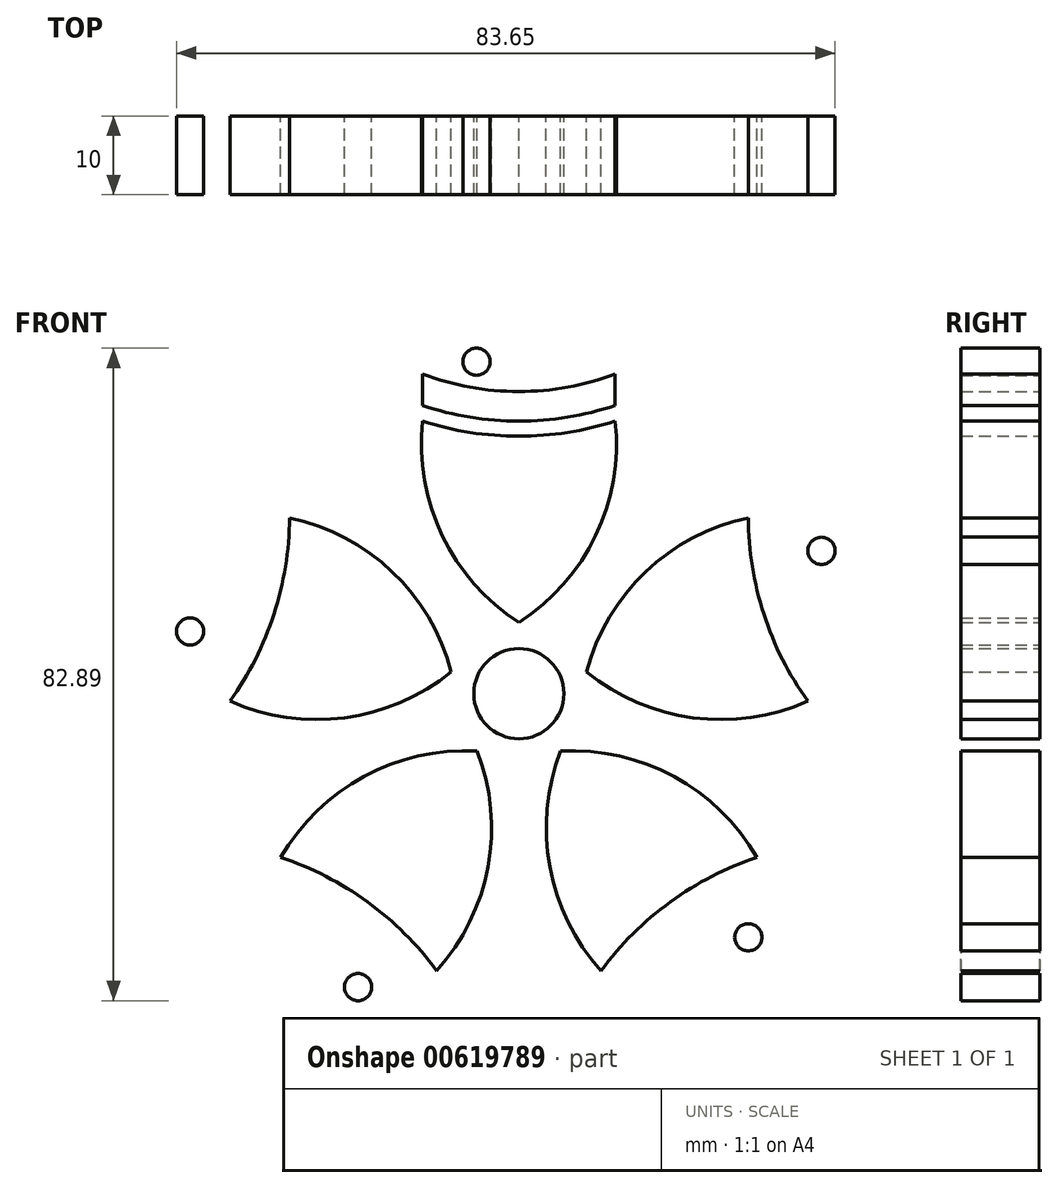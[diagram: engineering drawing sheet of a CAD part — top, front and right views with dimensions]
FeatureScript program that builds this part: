
annotation { "Feature Type Name" : "Feature", "Feature Type Description" : "" }
export const myFeature = defineFeature(function(context is Context, id is Id, definition is map)
    precondition{}
    {
        {
            var Q0;
            Q0=qCreatedBy(makeId("Front.planeOp"),FACE);
            var sketch = newSketch(context, id + "F0", { "sketchPlane" : qUnion([Q0])});
            skLineSegment(sketch, "E0", {"start": v(0, 45.42) * mm, "end": v(0, -45.42) * mm, "construction": true});
            skLineSegment(sketch, "E1", {"start": v(-45.42, 0) * mm, "end": v(45.42, 0) * mm, "construction": true});
            skCircle(sketch, "E2", {"center": v(0, 0) * mm, "radius": 5.72 * mm});
            skArc(sketch, "E3", {"start": v(-12.24, 34.62) * mm, "mid": v(-9.74, 20.09) * mm, "end": v(0, 9.03) * mm});
            skArc(sketch, "E4", {"start": v(-12.24, 34.62) * mm, "mid": v(-6.2, 33.19) * mm, "end": v(0, 32.72) * mm});
            skArc(sketch, "E5", {"start": v(-12.24, 36.62) * mm, "mid": v(-6.2, 35.11) * mm, "end": v(0, 34.62) * mm});
            skArc(sketch, "E6", {"start": v(-12.24, 40.62) * mm, "mid": v(-6.22, 38.94) * mm, "end": v(0, 38.38) * mm});
            skLineSegment(sketch, "E7", {"start": v(-12.24, 40.62) * mm, "end": v(-12.24, 36.62) * mm});
            skArc(sketch, "E8.MirrorCS", {"start": v(12.24, 34.62) * mm, "mid": v(9.74, 20.09) * mm, "end": v(0, 9.03) * mm});
            skArc(sketch, "E9.MirrorCS", {"start": v(12.24, 34.62) * mm, "mid": v(6.2, 33.19) * mm, "end": v(0, 32.72) * mm});
            skArc(sketch, "E10.MirrorCS", {"start": v(12.24, 36.62) * mm, "mid": v(6.2, 35.11) * mm, "end": v(0, 34.62) * mm});
            skArc(sketch, "E11.MirrorCS", {"start": v(12.24, 40.62) * mm, "mid": v(6.22, 38.94) * mm, "end": v(0, 38.38) * mm});
            skLineSegment(sketch, "E12.MirrorCS", {"start": v(12.24, 40.62) * mm, "end": v(12.24, 36.62) * mm});
            skArc(sketch, "E13.1.0", {"start": v(-36.7, -0.94) * mm, "mid": v(-33.48, 4.37) * mm, "end": v(-31.11, 10.1) * mm});
            skArc(sketch, "E13.1.1", {"start": v(-36.7, -0.94) * mm, "mid": v(-22.12, -3.06) * mm, "end": v(-8.59, 2.8) * mm});
            skArc(sketch, "E13.1.2", {"start": v(-29.14, 22.33) * mm, "mid": v(-16.1, 15.48) * mm, "end": v(-8.59, 2.8) * mm});
            skArc(sketch, "E13.1.3", {"start": v(-29.14, 22.33) * mm, "mid": v(-29.65, 16.14) * mm, "end": v(-31.11, 10.1) * mm});
            skArc(sketch, "E13.1.4", {"start": v(-31.04, 22.95) * mm, "mid": v(-31.48, 16.75) * mm, "end": v(-32.92, 10.7) * mm});
            skLineSegment(sketch, "E13.1.5", {"start": v(-34.85, 24.19) * mm, "end": v(-31.04, 22.95) * mm});
            skArc(sketch, "E13.1.6", {"start": v(-34.85, 24.19) * mm, "mid": v(-35.1, 17.95) * mm, "end": v(-36.5, 11.86) * mm});
            skArc(sketch, "E13.1.7", {"start": v(-42.4, 0.91) * mm, "mid": v(-38.95, 6.12) * mm, "end": v(-36.5, 11.86) * mm});
            skArc(sketch, "E13.1.8", {"start": v(-38.6, -0.32) * mm, "mid": v(-35.3, 4.95) * mm, "end": v(-32.92, 10.7) * mm});
            skLineSegment(sketch, "E13.1.9", {"start": v(-42.4, 0.91) * mm, "end": v(-38.6, -0.32) * mm});
            skArc(sketch, "E13.2.0", {"start": v(-10.45, -35.2) * mm, "mid": v(-14.5, -30.49) * mm, "end": v(-19.23, -26.47) * mm});
            skArc(sketch, "E13.2.1", {"start": v(-10.45, -35.2) * mm, "mid": v(-3.92, -21.98) * mm, "end": v(-5.3, -7.3) * mm});
            skArc(sketch, "E13.2.2", {"start": v(-30.25, -20.81) * mm, "mid": v(-19.7, -10.52) * mm, "end": v(-5.3, -7.3) * mm});
            skArc(sketch, "E13.2.3", {"start": v(-30.25, -20.81) * mm, "mid": v(-24.52, -23.2) * mm, "end": v(-19.23, -26.47) * mm});
            skArc(sketch, "E13.2.4", {"start": v(-31.42, -22.43) * mm, "mid": v(-25.65, -24.76) * mm, "end": v(-20.35, -28) * mm});
            skLineSegment(sketch, "E13.2.5", {"start": v(-33.77, -25.67) * mm, "end": v(-31.42, -22.43) * mm});
            skArc(sketch, "E13.2.6", {"start": v(-33.77, -25.67) * mm, "mid": v(-27.92, -27.84) * mm, "end": v(-22.56, -31.05) * mm});
            skArc(sketch, "E13.2.7", {"start": v(-13.97, -40.05) * mm, "mid": v(-17.85, -35.16) * mm, "end": v(-22.56, -31.05) * mm});
            skArc(sketch, "E13.2.8", {"start": v(-11.62, -36.81) * mm, "mid": v(-15.62, -32.05) * mm, "end": v(-20.35, -28) * mm});
            skLineSegment(sketch, "E13.2.9", {"start": v(-13.97, -40.05) * mm, "end": v(-11.62, -36.81) * mm});
            skArc(sketch, "E13.3.0", {"start": v(30.25, -20.81) * mm, "mid": v(24.52, -23.2) * mm, "end": v(19.23, -26.47) * mm});
            skArc(sketch, "E13.3.1", {"start": v(30.25, -20.81) * mm, "mid": v(19.7, -10.52) * mm, "end": v(5.3, -7.3) * mm});
            skArc(sketch, "E13.3.2", {"start": v(10.45, -35.2) * mm, "mid": v(3.92, -21.98) * mm, "end": v(5.3, -7.3) * mm});
            skArc(sketch, "E13.3.3", {"start": v(10.45, -35.2) * mm, "mid": v(14.5, -30.49) * mm, "end": v(19.23, -26.47) * mm});
            skArc(sketch, "E13.3.4", {"start": v(11.62, -36.81) * mm, "mid": v(15.62, -32.05) * mm, "end": v(20.35, -28) * mm});
            skLineSegment(sketch, "E13.3.5", {"start": v(13.97, -40.05) * mm, "end": v(11.62, -36.81) * mm});
            skArc(sketch, "E13.3.6", {"start": v(13.97, -40.05) * mm, "mid": v(17.85, -35.16) * mm, "end": v(22.56, -31.05) * mm});
            skArc(sketch, "E13.3.7", {"start": v(33.77, -25.67) * mm, "mid": v(27.92, -27.84) * mm, "end": v(22.56, -31.05) * mm});
            skArc(sketch, "E13.3.8", {"start": v(31.42, -22.43) * mm, "mid": v(25.65, -24.76) * mm, "end": v(20.35, -28) * mm});
            skLineSegment(sketch, "E13.3.9", {"start": v(33.77, -25.67) * mm, "end": v(31.42, -22.43) * mm});
            skArc(sketch, "E13.4.0", {"start": v(29.14, 22.33) * mm, "mid": v(29.65, 16.14) * mm, "end": v(31.11, 10.1) * mm});
            skArc(sketch, "E13.4.1", {"start": v(29.14, 22.33) * mm, "mid": v(16.1, 15.48) * mm, "end": v(8.59, 2.8) * mm});
            skArc(sketch, "E13.4.2", {"start": v(36.7, -0.94) * mm, "mid": v(22.12, -3.06) * mm, "end": v(8.59, 2.8) * mm});
            skArc(sketch, "E13.4.3", {"start": v(36.7, -0.94) * mm, "mid": v(33.48, 4.37) * mm, "end": v(31.11, 10.1) * mm});
            skArc(sketch, "E13.4.4", {"start": v(38.6, -0.32) * mm, "mid": v(35.3, 4.95) * mm, "end": v(32.92, 10.7) * mm});
            skLineSegment(sketch, "E13.4.5", {"start": v(42.4, 0.91) * mm, "end": v(38.6, -0.32) * mm});
            skArc(sketch, "E13.4.6", {"start": v(42.4, 0.91) * mm, "mid": v(38.95, 6.12) * mm, "end": v(36.5, 11.86) * mm});
            skArc(sketch, "E13.4.7", {"start": v(34.85, 24.19) * mm, "mid": v(35.1, 17.95) * mm, "end": v(36.5, 11.86) * mm});
            skArc(sketch, "E13.4.8", {"start": v(31.04, 22.95) * mm, "mid": v(31.48, 16.75) * mm, "end": v(32.92, 10.7) * mm});
            skLineSegment(sketch, "E13.4.9", {"start": v(34.85, 24.19) * mm, "end": v(31.04, 22.95) * mm});
            skCircle(sketch, "E14", {"center": v(-5.39, 42.17) * mm, "radius": 1.73 * mm});
            skCircle(sketch, "E15.MirrorC", {"center": v(5.39, 42.17) * mm, "radius": 1.73 * mm});
            skCircle(sketch, "E16.1.0", {"center": v(-41.77, 7.9) * mm, "radius": 1.73 * mm});
            skCircle(sketch, "E16.1.1", {"center": v(-38.44, 18.15) * mm, "radius": 1.73 * mm});
            skCircle(sketch, "E16.2.0", {"center": v(-20.43, -37.28) * mm, "radius": 1.73 * mm});
            skCircle(sketch, "E16.2.1", {"center": v(-29.14, -30.95) * mm, "radius": 1.73 * mm});
            skCircle(sketch, "E16.3.0", {"center": v(29.14, -30.95) * mm, "radius": 1.73 * mm});
            skCircle(sketch, "E16.3.1", {"center": v(20.43, -37.28) * mm, "radius": 1.73 * mm});
            skCircle(sketch, "E16.4.0", {"center": v(38.44, 18.15) * mm, "radius": 1.73 * mm});
            skCircle(sketch, "E16.4.1", {"center": v(41.77, 7.9) * mm, "radius": 1.73 * mm});
            skSolve(sketch);
        }
        {
            var Q0;
            Q0=makeQuery(id+"F0.imprint","IMPRINT",FACE,{"disambiguationData":[TD([[makeQuery(id+"F0.imprint","IMPRINT",EDGE,{"derivedFrom":sQuery(id+"F0.wireOp",EDGE,"E13.1.0")}),-1.0]])]});
            var Q1;
            Q1=makeQuery(id+"F0.imprint","IMPRINT",FACE,{"disambiguationData":[TD([[makeQuery(id+"F0.imprint","IMPRINT",EDGE,{"derivedFrom":sQuery(id+"F0.wireOp",EDGE,"E13.1.4")}),-1.0]])]});
            var Q2;
            Q2=makeQuery(id+"F0.imprint","IMPRINT",FACE,{"disambiguationData":[TD([[makeQuery(id+"F0.imprint","IMPRINT",EDGE,{"derivedFrom":sQuery(id+"F0.wireOp",EDGE,"E3")}),1.0]])]});
            var Q3;
            Q3=makeQuery(id+"F0.imprint","IMPRINT",FACE,{"disambiguationData":[TD([[makeQuery(id+"F0.imprint","IMPRINT",EDGE,{"derivedFrom":sQuery(id+"F0.wireOp",EDGE,"E5")}),1.0]])]});
            var Q4;
            Q4=makeQuery(id+"F0.imprint","IMPRINT",FACE,{"disambiguationData":[TD([[makeQuery(id+"F0.imprint","IMPRINT",EDGE,{"derivedFrom":sQuery(id+"F0.wireOp",EDGE,"E13.4.0")}),-1.0]])]});
            var Q5;
            Q5=makeQuery(id+"F0.imprint","IMPRINT",FACE,{"disambiguationData":[TD([[makeQuery(id+"F0.imprint","IMPRINT",EDGE,{"derivedFrom":sQuery(id+"F0.wireOp",EDGE,"E13.4.4")}),-1.0]])]});
            var Q6;
            Q6=makeQuery(id+"F0.imprint","IMPRINT",FACE,{"disambiguationData":[TD([[makeQuery(id+"F0.imprint","IMPRINT",EDGE,{"derivedFrom":sQuery(id+"F0.wireOp",EDGE,"E13.3.0")}),-1.0]])]});
            var Q7;
            Q7=makeQuery(id+"F0.imprint","IMPRINT",FACE,{"disambiguationData":[TD([[makeQuery(id+"F0.imprint","IMPRINT",EDGE,{"derivedFrom":sQuery(id+"F0.wireOp",EDGE,"E13.3.4")}),-1.0]])]});
            var Q8;
            Q8=makeQuery(id+"F0.imprint","IMPRINT",FACE,{"disambiguationData":[TD([[makeQuery(id+"F0.imprint","IMPRINT",EDGE,{"derivedFrom":sQuery(id+"F0.wireOp",EDGE,"E13.2.0")}),-1.0]])]});
            var Q9;
            Q9=makeQuery(id+"F0.imprint","IMPRINT",FACE,{"disambiguationData":[TD([[makeQuery(id+"F0.imprint","IMPRINT",EDGE,{"derivedFrom":sQuery(id+"F0.wireOp",EDGE,"E13.2.4")}),-1.0]])]});
            var Q10;
            Q10=makeQuery(id+"F0.imprint","IMPRINT",FACE,{"disambiguationData":[TD([[makeQuery(id+"F0.imprint","IMPRINT",EDGE,{"derivedFrom":sQuery(id+"F0.wireOp",EDGE,"E2")}),1.0]])]});
            var Q11;
            Q11=makeQuery(id+"F0.imprint","IMPRINT",FACE,{"disambiguationData":[TD([[makeQuery(id+"F0.imprint","IMPRINT",EDGE,{"derivedFrom":sQuery(id+"F0.wireOp",EDGE,"E14")}),1.0]])]});
            var Q12;
            Q12=makeQuery(id+"F0.imprint","IMPRINT",FACE,{"disambiguationData":[TD([[makeQuery(id+"F0.imprint","IMPRINT",EDGE,{"derivedFrom":sQuery(id+"F0.wireOp",EDGE,"E15.MirrorC")}),-1.0]])]});
            var Q13;
            Q13=makeQuery(id+"F0.imprint","IMPRINT",FACE,{"disambiguationData":[TD([[makeQuery(id+"F0.imprint","IMPRINT",EDGE,{"derivedFrom":sQuery(id+"F0.wireOp",EDGE,"E16.4.0")}),1.0]])]});
            var Q14;
            Q14=makeQuery(id+"F0.imprint","IMPRINT",FACE,{"disambiguationData":[TD([[makeQuery(id+"F0.imprint","IMPRINT",EDGE,{"derivedFrom":sQuery(id+"F0.wireOp",EDGE,"E16.4.1")}),-1.0]])]});
            var Q15;
            Q15=makeQuery(id+"F0.imprint","IMPRINT",FACE,{"disambiguationData":[TD([[makeQuery(id+"F0.imprint","IMPRINT",EDGE,{"derivedFrom":sQuery(id+"F0.wireOp",EDGE,"E16.3.0")}),1.0]])]});
            var Q16;
            Q16=makeQuery(id+"F0.imprint","IMPRINT",FACE,{"disambiguationData":[TD([[makeQuery(id+"F0.imprint","IMPRINT",EDGE,{"derivedFrom":sQuery(id+"F0.wireOp",EDGE,"E16.3.1")}),-1.0]])]});
            var Q17;
            Q17=makeQuery(id+"F0.imprint","IMPRINT",FACE,{"disambiguationData":[TD([[makeQuery(id+"F0.imprint","IMPRINT",EDGE,{"derivedFrom":sQuery(id+"F0.wireOp",EDGE,"E16.2.0")}),1.0]])]});
            var Q18;
            Q18=makeQuery(id+"F0.imprint","IMPRINT",FACE,{"disambiguationData":[TD([[makeQuery(id+"F0.imprint","IMPRINT",EDGE,{"derivedFrom":sQuery(id+"F0.wireOp",EDGE,"E16.2.1")}),-1.0]])]});
            var Q19;
            Q19=makeQuery(id+"F0.imprint","IMPRINT",FACE,{"disambiguationData":[TD([[makeQuery(id+"F0.imprint","IMPRINT",EDGE,{"derivedFrom":sQuery(id+"F0.wireOp",EDGE,"E16.1.0")}),1.0]])]});
            var Q20;
            Q20=makeQuery(id+"F0.imprint","IMPRINT",FACE,{"disambiguationData":[TD([[makeQuery(id+"F0.imprint","IMPRINT",EDGE,{"derivedFrom":sQuery(id+"F0.wireOp",EDGE,"E16.1.1")}),-1.0]])]});
            extrude(context, id + "F1", {"entities" : qUnion([Q0, Q1, Q2, Q3, Q4, Q5, Q6, Q7, Q8, Q9, Q10, Q11, Q12, Q13, Q14, Q15, Q16, Q17, Q18, Q19, Q20]), "depth" : 10 * mm, "offsetDistance" : 25 * mm});
        }
    });
